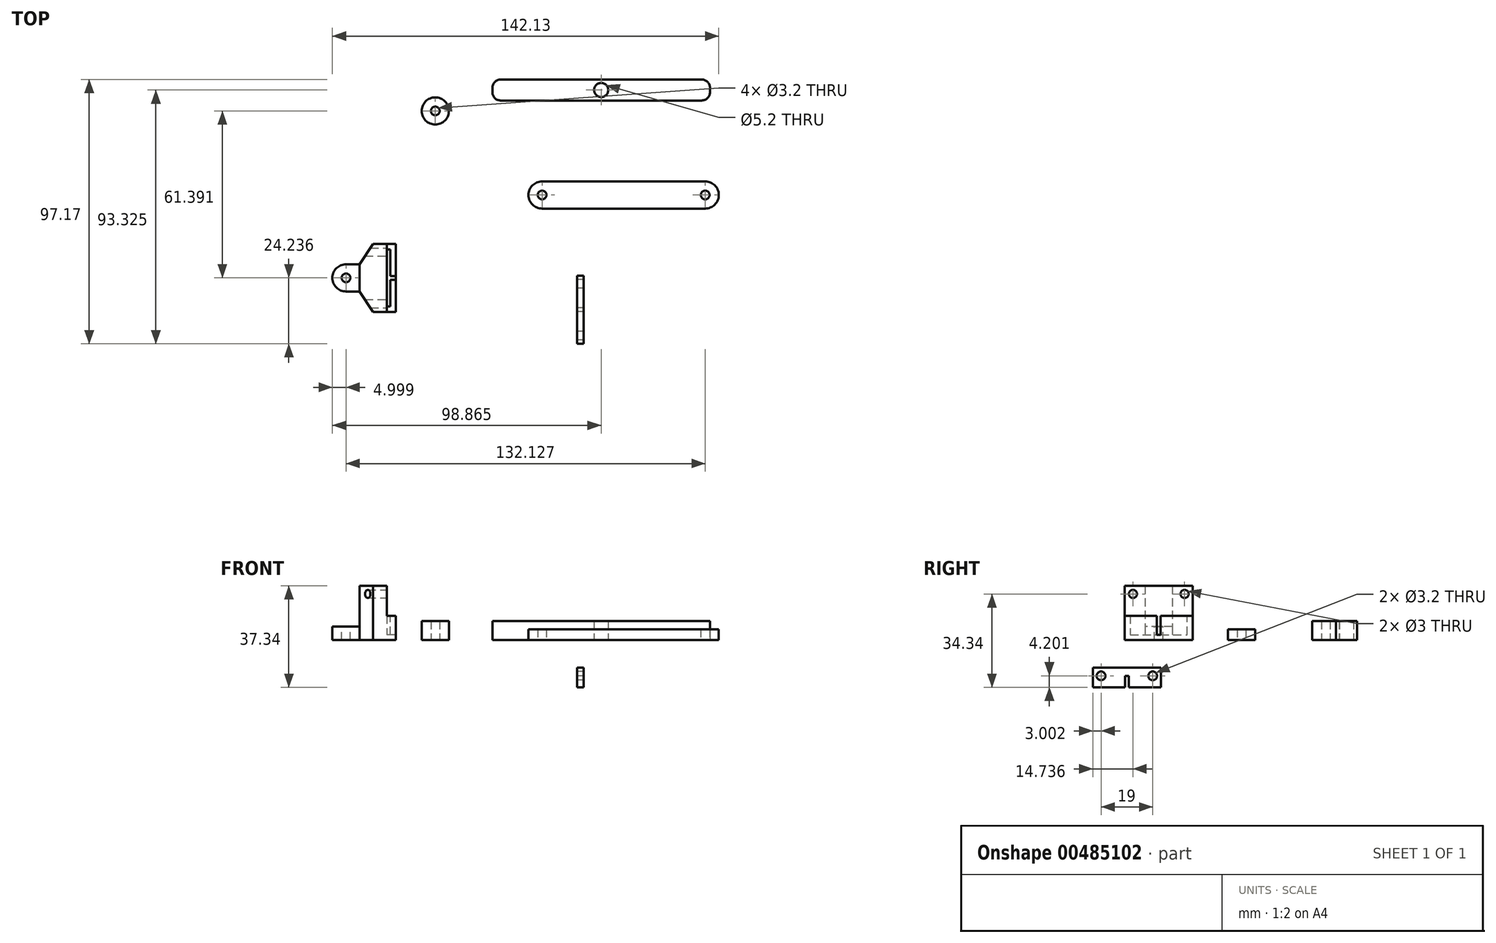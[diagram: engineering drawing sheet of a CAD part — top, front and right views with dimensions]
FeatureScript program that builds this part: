
annotation { "Feature Type Name" : "Feature", "Feature Type Description" : "" }
export const myFeature = defineFeature(function(context is Context, id is Id, definition is map)
    precondition{}
    {
        {
            var Q0;
            Q0=qCreatedBy(makeId("Top.planeOp"),FACE);
            var sketch = newSketch(context, id + "F0", { "sketchPlane" : qUnion([Q0])});
            skLineSegment(sketch, "E0.bottom", {"start": v(-17.82, 2.81) * mm, "end": v(52.18, 2.81) * mm});
            skLineSegment(sketch, "E0.top", {"start": v(-17.82, -7.19) * mm, "end": v(52.18, -7.19) * mm});
            skLineSegment(sketch, "E0.left", {"start": v(-17.82, 2.81) * mm, "end": v(-17.82, -7.19) * mm});
            skLineSegment(sketch, "E0.right", {"start": v(52.18, 2.81) * mm, "end": v(52.18, -7.19) * mm});
            skLineSegment(sketch, "E1", {"start": v(-12.82, 2.81) * mm, "end": v(-12.82, -7.19) * mm, "construction": true});
            skLineSegment(sketch, "E2", {"start": v(47.18, 2.81) * mm, "end": v(47.18, -7.19) * mm, "construction": true});
            skCircle(sketch, "E3", {"center": v(-12.82, -2.19) * mm, "radius": 1.6 * mm});
            skCircle(sketch, "E4", {"center": v(47.18, -2.19) * mm, "radius": 1.6 * mm});
            skSolve(sketch);
        }
        {
            var Q0;
            Q0=makeQuery(id+"F0.imprint","IMPRINT",FACE,{"disambiguationData":[TD([[makeQuery(id+"F0.imprint","IMPRINT",EDGE,{"derivedFrom":sQuery(id+"F0.wireOp",EDGE,"E0.bottom")}),-1.0]])]});
            extrude(context, id + "F1", {"entities" : qUnion([Q0]), "depth" : 4 * mm, "offsetDistance" : 25 * mm});
        }
        {
            var Q0;
            Q0=makeQuery(id+"F1.opExtrude","SWEPT_EDGE",EDGE,{"disambiguationData":[OSD([sQuery(id+"F0.wireOp",EDGE,"E0.bottom"),sQuery(id+"F0.wireOp",EDGE,"E0.left")])]});
            var Q1;
            Q1=makeQuery(id+"F1.opExtrude","SWEPT_EDGE",EDGE,{"disambiguationData":[OSD([sQuery(id+"F0.wireOp",EDGE,"E0.top"),sQuery(id+"F0.wireOp",EDGE,"E0.left")])]});
            var Q2;
            Q2=makeQuery(id+"F1.opExtrude","SWEPT_EDGE",EDGE,{"disambiguationData":[OSD([sQuery(id+"F0.wireOp",EDGE,"E0.bottom"),sQuery(id+"F0.wireOp",EDGE,"E0.right")])]});
            var Q3;
            Q3=makeQuery(id+"F1.opExtrude","SWEPT_EDGE",EDGE,{"disambiguationData":[OSD([sQuery(id+"F0.wireOp",EDGE,"E0.top"),sQuery(id+"F0.wireOp",EDGE,"E0.right")])]});
            fillet(context, id + "F2", {"entities" : qUnion([Q0, Q1, Q2, Q3]), "radius" : 5 * mm, "tangentPropagation" : true, "allowEdgeOverflow" : false});
        }
        {
            var Q0;
            Q0=qCreatedBy(makeId("Top.planeOp"),FACE);
            var sketch = newSketch(context, id + "F3", { "sketchPlane" : qUnion([Q0])});
            skCircle(sketch, "E5", {"center": v(-52.1, 28.72) * mm, "radius": 5 * mm});
            skCircle(sketch, "E6", {"center": v(-52.1, 28.72) * mm, "radius": 1.6 * mm});
            skSolve(sketch);
        }
        {
            var Q0;
            Q0=makeQuery(id+"F3.imprint","IMPRINT",FACE,{"disambiguationData":[TD([[makeQuery(id+"F3.imprint","IMPRINT",EDGE,{"derivedFrom":sQuery(id+"F3.wireOp",EDGE,"E5")}),1.0]])]});
            extrude(context, id + "F4", {"entities" : qUnion([Q0]), "depth" : 7 * mm, "offsetDistance" : 25 * mm});
        }
        {
            var Q0;
            Q0=qCreatedBy(makeId("Top.planeOp"),FACE);
            var sketch = newSketch(context, id + "F5", { "sketchPlane" : qUnion([Q0])});
            skCircle(sketch, "E7", {"center": v(8.91, 36.41) * mm, "radius": 9 * mm});
            skCircle(sketch, "E8", {"center": v(8.91, 36.41) * mm, "radius": 2.6 * mm});
            skLineSegment(sketch, "E9.bottom", {"start": v(-31.09, 40.26) * mm, "end": v(48.91, 40.26) * mm});
            skLineSegment(sketch, "E9.top", {"start": v(-31.09, 32.57) * mm, "end": v(48.91, 32.57) * mm});
            skLineSegment(sketch, "E9.left", {"start": v(-31.09, 40.26) * mm, "end": v(-31.09, 32.57) * mm});
            skLineSegment(sketch, "E9.right", {"start": v(48.91, 40.26) * mm, "end": v(48.91, 32.57) * mm});
            skSolve(sketch);
        }
        {
            var Q0;
            Q0=qCreatedBy(makeId("Top.planeOp"),FACE);
            var sketch = newSketch(context, id + "F6", { "sketchPlane" : qUnion([Q0])});
            skLineSegment(sketch, "E10.bottom", {"start": v(-74.95, -20.17) * mm, "end": v(-69.95, -20.17) * mm, "construction": true});
            skLineSegment(sketch, "E10.top", {"start": v(-74.95, -45.17) * mm, "end": v(-69.95, -45.17) * mm, "construction": true});
            skLineSegment(sketch, "E10.left", {"start": v(-74.95, -20.17) * mm, "end": v(-74.95, -45.17) * mm, "construction": true});
            skLineSegment(sketch, "E10.right", {"start": v(-69.95, -20.17) * mm, "end": v(-69.95, -45.17) * mm, "construction": true});
            skLineSegment(sketch, "E11.bottom", {"start": v(-69.95, -27.67) * mm, "end": v(-89.95, -27.67) * mm, "construction": true});
            skLineSegment(sketch, "E11.top", {"start": v(-69.95, -37.67) * mm, "end": v(-89.95, -37.67) * mm, "construction": true});
            skLineSegment(sketch, "E11.left", {"start": v(-69.95, -27.67) * mm, "end": v(-69.95, -37.67) * mm, "construction": true});
            skLineSegment(sketch, "E11.right", {"start": v(-89.95, -27.67) * mm, "end": v(-89.95, -37.67) * mm, "construction": true});
            skLineSegment(sketch, "E12", {"start": v(-89.95, -27.67) * mm, "end": v(-79.95, -27.67) * mm});
            skLineSegment(sketch, "E13", {"start": v(-79.95, -27.67) * mm, "end": v(-74.95, -20.17) * mm});
            skLineSegment(sketch, "E14", {"start": v(-69.95, -20.17) * mm, "end": v(-74.95, -20.17) * mm});
            skLineSegment(sketch, "E15", {"start": v(-69.95, -20.17) * mm, "end": v(-69.95, -45.17) * mm});
            skLineSegment(sketch, "E16", {"start": v(-69.95, -45.17) * mm, "end": v(-74.95, -45.17) * mm});
            skLineSegment(sketch, "E17", {"start": v(-74.95, -45.17) * mm, "end": v(-79.95, -37.67) * mm});
            skLineSegment(sketch, "E18", {"start": v(-79.95, -37.67) * mm, "end": v(-89.95, -37.67) * mm});
            skLineSegment(sketch, "E19", {"start": v(-89.95, -37.67) * mm, "end": v(-89.95, -27.67) * mm});
            skLineSegment(sketch, "E20", {"start": v(-79.95, -27.67) * mm, "end": v(-79.95, -37.67) * mm});
            skSolve(sketch);
        }
        {
            var Q0;
            Q0=makeQuery(id+"F6.imprint","IMPRINT",FACE,{"disambiguationData":[TD([[makeQuery(id+"F6.imprint","IMPRINT",EDGE,{"derivedFrom":sQuery(id+"F6.wireOp",EDGE,"E13")}),-1.0]])]});
            extrude(context, id + "F7", {"entities" : qUnion([Q0]), "depth" : 20 * mm, "offsetDistance" : 25 * mm});
        }
        {
            var Q0;
            Q0=makeQuery(id+"F6.imprint","IMPRINT",FACE,{"disambiguationData":[TD([[makeQuery(id+"F6.imprint","IMPRINT",EDGE,{"derivedFrom":sQuery(id+"F6.wireOp",EDGE,"E12")}),-1.0]])]});
            extrude(context, id + "F8", {"entities" : qUnion([Q0]), "operationType" : NewBodyOperationType.ADD, "depth" : 5 * mm, "offsetDistance" : 25 * mm});
        }
        {
            var Q0;
            Q0=makeQuery(id+"F8.opExtrude","CAP_FACE",FACE,{"disambiguationData":[OSD([sQuery(id+"F6.wireOp",EDGE,"E12"),sQuery(id+"F6.wireOp",EDGE,"E18"),sQuery(id+"F6.wireOp",EDGE,"E19"),sQuery(id+"F6.wireOp",EDGE,"E20")])],"isStart":false});
            var sketch = newSketch(context, id + "F9", { "sketchPlane" : qUnion([Q0])});
            skLineSegment(sketch, "E21", {"start": v(-84.95, -27.67) * mm, "end": v(-84.95, -37.67) * mm, "construction": true});
            skCircle(sketch, "E22", {"center": v(-84.95, -32.67) * mm, "radius": 1.6 * mm, "construction": true});
            skSolve(sketch);
        }
        {
            var Q0;
            Q0=sQuery(id+"F9.wireOp",VERTEX,"E22.center");
            var Q1;
            Q1=makeQuery(id+"F7.opExtrude","SWEPT_BODY",BODY,{"disambiguationData":[OSD([sQuery(id+"F6.wireOp",EDGE,"E13"),sQuery(id+"F6.wireOp",EDGE,"E14"),sQuery(id+"F6.wireOp",EDGE,"E15"),sQuery(id+"F6.wireOp",EDGE,"E16"),sQuery(id+"F6.wireOp",EDGE,"E17"),sQuery(id+"F6.wireOp",EDGE,"E20")])]});
            hole(context, id + "F10", {"style" : HoleStyle.SIMPLE, "endStyle" : HoleEndStyle.BLIND, "holeDiameter" : 3.2 * mm, "holeDepth" : 5 * mm, "isTappedThrough" : true, "tappedDepth" : 12 * mm, "tapClearance" : 3, "locations" : qUnion([Q0]), "scope" : qUnion([Q1])});
        }
        {
            var Q0;
            Q0=makeQuery(id+"F8.opExtrude","SWEPT_EDGE",EDGE,{"disambiguationData":[OSD([sQuery(id+"F6.wireOp",EDGE,"E18"),sQuery(id+"F6.wireOp",EDGE,"E19")])]});
            var Q1;
            Q1=makeQuery(id+"F8.opExtrude","SWEPT_EDGE",EDGE,{"disambiguationData":[OSD([sQuery(id+"F6.wireOp",EDGE,"E12"),sQuery(id+"F6.wireOp",EDGE,"E19")])]});
            fillet(context, id + "F11", {"entities" : qUnion([Q0, Q1]), "radius" : 5 * mm, "tangentPropagation" : true, "allowEdgeOverflow" : false});
        }
        {
            var Q0;
            Q0=makeQuery(id+"F7.opExtrude","SWEPT_FACE",FACE,{"disambiguationData":[OSD([sQuery(id+"F6.wireOp",EDGE,"E15")])]});
            var sketch = newSketch(context, id + "F12", { "sketchPlane" : qUnion([Q0])});
            skLineSegment(sketch, "E23.bottom", {"start": v(-45.17, 20) * mm, "end": v(-20.17, 20) * mm});
            skLineSegment(sketch, "E23.top", {"start": v(-45.17, 0) * mm, "end": v(-20.17, 0) * mm});
            skLineSegment(sketch, "E23.left", {"start": v(-45.17, 20) * mm, "end": v(-45.17, 0) * mm});
            skLineSegment(sketch, "E23.right", {"start": v(-20.17, 20) * mm, "end": v(-20.17, 0) * mm});
            skLineSegment(sketch, "E24.bottom", {"start": v(-45.17, 9) * mm, "end": v(-43.17, 9) * mm, "construction": true});
            skLineSegment(sketch, "E24.top", {"start": v(-45.17, 0) * mm, "end": v(-43.17, 0) * mm, "construction": true});
            skLineSegment(sketch, "E24.left", {"start": v(-45.17, 9) * mm, "end": v(-45.17, 0) * mm, "construction": true});
            skLineSegment(sketch, "E24.right", {"start": v(-43.17, 9) * mm, "end": v(-43.17, 0) * mm, "construction": true});
            skLineSegment(sketch, "E25.bottom", {"start": v(-45.17, 2) * mm, "end": v(-20.17, 2) * mm, "construction": true});
            skLineSegment(sketch, "E25.top", {"start": v(-45.17, 0) * mm, "end": v(-20.17, 0) * mm, "construction": true});
            skLineSegment(sketch, "E25.left", {"start": v(-45.17, 2) * mm, "end": v(-45.17, 0) * mm, "construction": true});
            skLineSegment(sketch, "E25.right", {"start": v(-20.17, 2) * mm, "end": v(-20.17, 0) * mm, "construction": true});
            skLineSegment(sketch, "E26.bottom", {"start": v(-20.17, 0) * mm, "end": v(-22.17, 0) * mm, "construction": true});
            skLineSegment(sketch, "E26.top", {"start": v(-20.17, 9) * mm, "end": v(-22.17, 9) * mm, "construction": true});
            skLineSegment(sketch, "E26.left", {"start": v(-20.17, 0) * mm, "end": v(-20.17, 9) * mm, "construction": true});
            skLineSegment(sketch, "E26.right", {"start": v(-22.17, 0) * mm, "end": v(-22.17, 9) * mm, "construction": true});
            skLineSegment(sketch, "E27", {"start": v(-45.17, 9) * mm, "end": v(-43.17, 9) * mm});
            skLineSegment(sketch, "E28", {"start": v(-43.17, 9) * mm, "end": v(-43.17, 2) * mm});
            skLineSegment(sketch, "E29", {"start": v(-43.17, 2) * mm, "end": v(-22.17, 2) * mm});
            skLineSegment(sketch, "E30", {"start": v(-22.17, 2) * mm, "end": v(-22.17, 9) * mm});
            skLineSegment(sketch, "E31", {"start": v(-22.17, 9) * mm, "end": v(-20.17, 9) * mm});
            skLineSegment(sketch, "E32", {"start": v(-20.17, 9) * mm, "end": v(-20.17, 0) * mm});
            skLineSegment(sketch, "E33", {"start": v(-20.17, 0) * mm, "end": v(-45.17, 0) * mm});
            skLineSegment(sketch, "E34", {"start": v(-45.17, 0) * mm, "end": v(-45.17, 9) * mm});
            skLineSegment(sketch, "E35", {"start": v(-42.17, 20) * mm, "end": v(-42.17, 2) * mm, "construction": true});
            skLineSegment(sketch, "E36", {"start": v(-23.17, 20) * mm, "end": v(-23.17, 2) * mm, "construction": true});
            skLineSegment(sketch, "E37", {"start": v(-45.17, 17) * mm, "end": v(-20.17, 17) * mm, "construction": true});
            skCircle(sketch, "E38", {"center": v(-42.17, 17) * mm, "radius": 1.5 * mm, "construction": true});
            skCircle(sketch, "E39", {"center": v(-23.17, 17) * mm, "radius": 1.5 * mm, "construction": true});
            skSolve(sketch);
        }
        {
            var Q0;
            Q0=makeQuery(id+"F12.imprint","IMPRINT",FACE,{"disambiguationData":[TD([[makeQuery(id+"F12.imprint","IMPRINT",EDGE,{"derivedFrom":sQuery(id+"F12.wireOp",EDGE,"E27")}),-1.0]])]});
            extrude(context, id + "F13", {"entities" : qUnion([Q0]), "operationType" : NewBodyOperationType.ADD, "depth" : 1.3 * mm, "offsetDistance" : 25 * mm});
        }
        {
            var Q0;
            Q0=makeQuery(id+"F13.opExtrude","CAP_FACE",FACE,{"disambiguationData":[OSD([sQuery(id+"F12.wireOp",EDGE,"E27"),sQuery(id+"F12.wireOp",EDGE,"E28"),sQuery(id+"F12.wireOp",EDGE,"E29"),sQuery(id+"F12.wireOp",EDGE,"E30"),sQuery(id+"F12.wireOp",EDGE,"E31"),sQuery(id+"F12.wireOp",EDGE,"E32"),sQuery(id+"F12.wireOp",EDGE,"E33"),sQuery(id+"F12.wireOp",EDGE,"E34")])],"isStart":false});
            var sketch = newSketch(context, id + "F14", { "sketchPlane" : qUnion([Q0])});
            skLineSegment(sketch, "E40.bottom", {"start": v(-45.17, 9) * mm, "end": v(-20.17, 9) * mm, "construction": true});
            skLineSegment(sketch, "E40.top", {"start": v(-45.17, 0) * mm, "end": v(-20.17, 0) * mm, "construction": true});
            skLineSegment(sketch, "E40.left", {"start": v(-45.17, 9) * mm, "end": v(-45.17, 0) * mm, "construction": true});
            skLineSegment(sketch, "E40.right", {"start": v(-20.17, 9) * mm, "end": v(-20.17, 0) * mm, "construction": true});
            skLineSegment(sketch, "E41", {"start": v(-33.37, 9) * mm, "end": v(-33.37, 2) * mm, "construction": true});
            skLineSegment(sketch, "E42", {"start": v(-31.97, 9) * mm, "end": v(-31.97, 2) * mm, "construction": true});
            skLineSegment(sketch, "E43", {"start": v(-45.17, 9) * mm, "end": v(-33.37, 9) * mm});
            skLineSegment(sketch, "E44", {"start": v(-33.37, 9) * mm, "end": v(-33.37, 2) * mm});
            skLineSegment(sketch, "E45", {"start": v(-33.37, 2) * mm, "end": v(-31.97, 2) * mm});
            skLineSegment(sketch, "E46", {"start": v(-31.97, 2) * mm, "end": v(-31.97, 9) * mm});
            skLineSegment(sketch, "E47", {"start": v(-31.97, 9) * mm, "end": v(-20.17, 9) * mm});
            skLineSegment(sketch, "E48", {"start": v(-20.17, 9) * mm, "end": v(-20.17, 0) * mm});
            skLineSegment(sketch, "E49", {"start": v(-20.17, 0) * mm, "end": v(-45.17, 0) * mm});
            skLineSegment(sketch, "E50", {"start": v(-45.17, 0) * mm, "end": v(-45.17, 9) * mm});
            skSolve(sketch);
        }
        {
            var Q0;
            {var subQ1=sQuery(id+"F14.wireOp",EDGE,"E45");Q0=makeQuery(id+"F14.imprint","IMPRINT",FACE,{"disambiguationData":[TD([[makeQuery(id+"F14.imprint","IMPRINT",EDGE,{"derivedFrom":subQ1}),-1.0]])]});}
            var Q1;
            {var subQ2=sQuery(id+"F14.wireOp",EDGE,"E44");Q1=makeQuery(id+"F14.imprint","IMPRINT",FACE,{"disambiguationData":[TD([[makeQuery(id+"F14.imprint","IMPRINT",EDGE,{"derivedFrom":subQ2}),-1.0]])]});}
            var Q2;
            {var subQ0=sQuery(id+"F14.wireOp",EDGE,"E46");Q2=makeQuery(id+"F14.imprint","IMPRINT",FACE,{"disambiguationData":[TD([[makeQuery(id+"F14.imprint","IMPRINT",EDGE,{"derivedFrom":subQ0}),-1.0]])]});}
            extrude(context, id + "F15", {"entities" : qUnion([Q0, Q1, Q2]), "operationType" : NewBodyOperationType.ADD, "depth" : 2 * mm, "offsetDistance" : 25 * mm});
        }
        {
            var Q0;
            Q0=sQuery(id+"F12.wireOp",VERTEX,"E38.center");
            var Q1;
            Q1=sQuery(id+"F12.wireOp",VERTEX,"E39.center");
            var Q2;
            Q2=makeQuery(id+"F7.opExtrude","SWEPT_BODY",BODY,{"disambiguationData":[OSD([sQuery(id+"F6.wireOp",EDGE,"E13"),sQuery(id+"F6.wireOp",EDGE,"E14"),sQuery(id+"F6.wireOp",EDGE,"E15"),sQuery(id+"F6.wireOp",EDGE,"E16"),sQuery(id+"F6.wireOp",EDGE,"E17"),sQuery(id+"F6.wireOp",EDGE,"E20")])]});
            hole(context, id + "F16", {"style" : HoleStyle.SIMPLE, "endStyle" : HoleEndStyle.BLIND, "holeDiameter" : 3 * mm, "holeDepth" : 10 * mm, "isTappedThrough" : true, "tappedDepth" : 12 * mm, "tapClearance" : 3, "locations" : qUnion([Q0, Q1]), "scope" : qUnion([Q2])});
        }
        {
            var Q0;
            Q0=qCreatedBy(makeId("Right.planeOp"),FACE);
            var sketch = newSketch(context, id + "F17", { "sketchPlane" : qUnion([Q0])});
            skLineSegment(sketch, "E51.bottom", {"start": v(-56.9, -10.14) * mm, "end": v(-31.9, -10.14) * mm});
            skLineSegment(sketch, "E51.top", {"start": v(-56.9, -27.08) * mm, "end": v(-31.9, -27.08) * mm, "construction": true});
            skLineSegment(sketch, "E51.left", {"start": v(-56.9, -10.14) * mm, "end": v(-56.9, -27.08) * mm, "construction": true});
            skLineSegment(sketch, "E51.right", {"start": v(-31.9, -10.14) * mm, "end": v(-31.9, -27.08) * mm, "construction": true});
            skLineSegment(sketch, "E52.bottom", {"start": v(-56.9, -10.14) * mm, "end": v(-31.9, -10.14) * mm, "construction": true});
            skLineSegment(sketch, "E52.top", {"start": v(-56.9, -17.34) * mm, "end": v(-31.9, -17.34) * mm, "construction": true});
            skLineSegment(sketch, "E52.left", {"start": v(-56.9, -10.14) * mm, "end": v(-56.9, -17.34) * mm, "construction": true});
            skLineSegment(sketch, "E52.right", {"start": v(-31.9, -10.14) * mm, "end": v(-31.9, -17.34) * mm, "construction": true});
            skLineSegment(sketch, "E53", {"start": v(-45.1, -17.34) * mm, "end": v(-45.1, -10.14) * mm, "construction": true});
            skLineSegment(sketch, "E54", {"start": v(-43.7, -17.34) * mm, "end": v(-43.7, -10.14) * mm, "construction": true});
            skLineSegment(sketch, "E55", {"start": v(-56.9, -13.14) * mm, "end": v(-31.9, -13.14) * mm, "construction": true});
            skLineSegment(sketch, "E56", {"start": v(-56.9, -12.14) * mm, "end": v(-31.9, -12.14) * mm, "construction": true});
            skLineSegment(sketch, "E57", {"start": v(-34.9, -10.14) * mm, "end": v(-34.9, -17.34) * mm, "construction": true});
            skLineSegment(sketch, "E58", {"start": v(-53.9, -10.14) * mm, "end": v(-53.9, -17.34) * mm, "construction": true});
            skCircle(sketch, "E59", {"center": v(-53.9, -13.14) * mm, "radius": 1.6 * mm});
            skCircle(sketch, "E60", {"center": v(-34.9, -13.14) * mm, "radius": 1.6 * mm});
            skLineSegment(sketch, "E61", {"start": v(-56.9, -10.14) * mm, "end": v(-56.9, -17.34) * mm});
            skLineSegment(sketch, "E62", {"start": v(-45.1, -17.34) * mm, "end": v(-56.9, -17.34) * mm});
            skLineSegment(sketch, "E63", {"start": v(-45.1, -17.34) * mm, "end": v(-45.1, -13.14) * mm});
            skLineSegment(sketch, "E64", {"start": v(-45.1, -13.14) * mm, "end": v(-43.7, -13.14) * mm});
            skPoint(sketch, "E64.endSnap0", {"position": v(-44.4, -13.14) * mm});
            skLineSegment(sketch, "E65", {"start": v(-43.7, -13.14) * mm, "end": v(-43.7, -17.34) * mm});
            skLineSegment(sketch, "E66", {"start": v(-43.7, -17.34) * mm, "end": v(-31.9, -17.34) * mm});
            skLineSegment(sketch, "E67", {"start": v(-31.9, -17.34) * mm, "end": v(-31.9, -10.14) * mm});
            skSolve(sketch);
        }
        {
            var Q0;
            Q0=makeQuery(id+"F17.imprint","IMPRINT",FACE,{"disambiguationData":[TD([[makeQuery(id+"F17.imprint","IMPRINT",EDGE,{"derivedFrom":sQuery(id+"F17.wireOp",EDGE,"E51.bottom")}),-1.0]])]});
            extrude(context, id + "F18", {"entities" : qUnion([Q0]), "depth" : 2.5 * mm, "offsetDistance" : 25 * mm});
        }
        {
            var Q0;
            {var subQ5=sQuery(id+"F5.wireOp",EDGE,"E9.left");Q0=makeQuery(id+"F5.imprint","IMPRINT",FACE,{"disambiguationData":[TD([[makeQuery(id+"F5.imprint","IMPRINT",EDGE,{"derivedFrom":subQ5}),1.0]])]});}
            var Q1;
            Q1=makeQuery(id+"F5.imprint","IMPRINT",FACE,{"disambiguationData":[TD([[makeQuery(id+"F5.imprint","IMPRINT",EDGE,{"derivedFrom":sQuery(id+"F5.wireOp",EDGE,"E8")}),-1.0]])]});
            var Q2;
            {var subQ0=sQuery(id+"F5.wireOp",EDGE,"E9.bottom");var subQ1=sQuery(id+"F5.wireOp",EDGE,"E7");var subQ2=makeQuery(id+"F5.imprint","INTERSECT",VERTEX,{"disambiguationData":[OD(0.0)],"derivedFrom":[subQ1,subQ0]});Q2=makeQuery(id+"F5.imprint","IMPRINT",FACE,{"disambiguationData":[TD([[makeQuery(id+"F5.imprint","IMPRINT",EDGE,{"disambiguationData":[TD([[subQ2,1.0]])],"derivedFrom":subQ1}),1.0]])]});}
            var Q3;
            {var subQ0=sQuery(id+"F5.wireOp",EDGE,"E9.top");var subQ1=sQuery(id+"F5.wireOp",EDGE,"E7");var subQ2=makeQuery(id+"F5.imprint","INTERSECT",VERTEX,{"disambiguationData":[OD(0.0)],"derivedFrom":[subQ1,subQ0]});Q3=makeQuery(id+"F5.imprint","IMPRINT",FACE,{"disambiguationData":[TD([[makeQuery(id+"F5.imprint","IMPRINT",EDGE,{"disambiguationData":[TD([[subQ2,-1.0]])],"derivedFrom":subQ1}),1.0]])]});}
            var Q4;
            {var subQ5=sQuery(id+"F5.wireOp",EDGE,"E9.right");Q4=makeQuery(id+"F5.imprint","IMPRINT",FACE,{"disambiguationData":[TD([[makeQuery(id+"F5.imprint","IMPRINT",EDGE,{"derivedFrom":subQ5}),-1.0]])]});}
            extrude(context, id + "F19", {"entities" : qUnion([Q0, Q1, Q2, Q3, Q4]), "depth" : 7 * mm, "offsetDistance" : 25 * mm});
        }
        {
            var Q0;
            Q0=makeQuery(id+"F19.opExtrude","SWEPT_EDGE",EDGE,{"disambiguationData":[OSD([sQuery(id+"F5.wireOp",EDGE,"E9.bottom"),sQuery(id+"F5.wireOp",EDGE,"E9.left")])]});
            var Q1;
            Q1=makeQuery(id+"F19.opExtrude","SWEPT_EDGE",EDGE,{"disambiguationData":[OSD([sQuery(id+"F5.wireOp",EDGE,"E9.top"),sQuery(id+"F5.wireOp",EDGE,"E9.left")])]});
            var Q2;
            Q2=makeQuery(id+"F19.opExtrude","SWEPT_EDGE",EDGE,{"disambiguationData":[OSD([sQuery(id+"F5.wireOp",EDGE,"E9.bottom"),sQuery(id+"F5.wireOp",EDGE,"E9.right")])]});
            var Q3;
            Q3=makeQuery(id+"F19.opExtrude","SWEPT_EDGE",EDGE,{"disambiguationData":[OSD([sQuery(id+"F5.wireOp",EDGE,"E9.top"),sQuery(id+"F5.wireOp",EDGE,"E9.right")])]});
            fillet(context, id + "F20", {"entities" : qUnion([Q0, Q1, Q2, Q3]), "radius" : 3 * mm, "tangentPropagation" : true, "allowEdgeOverflow" : false});
        }
    });
